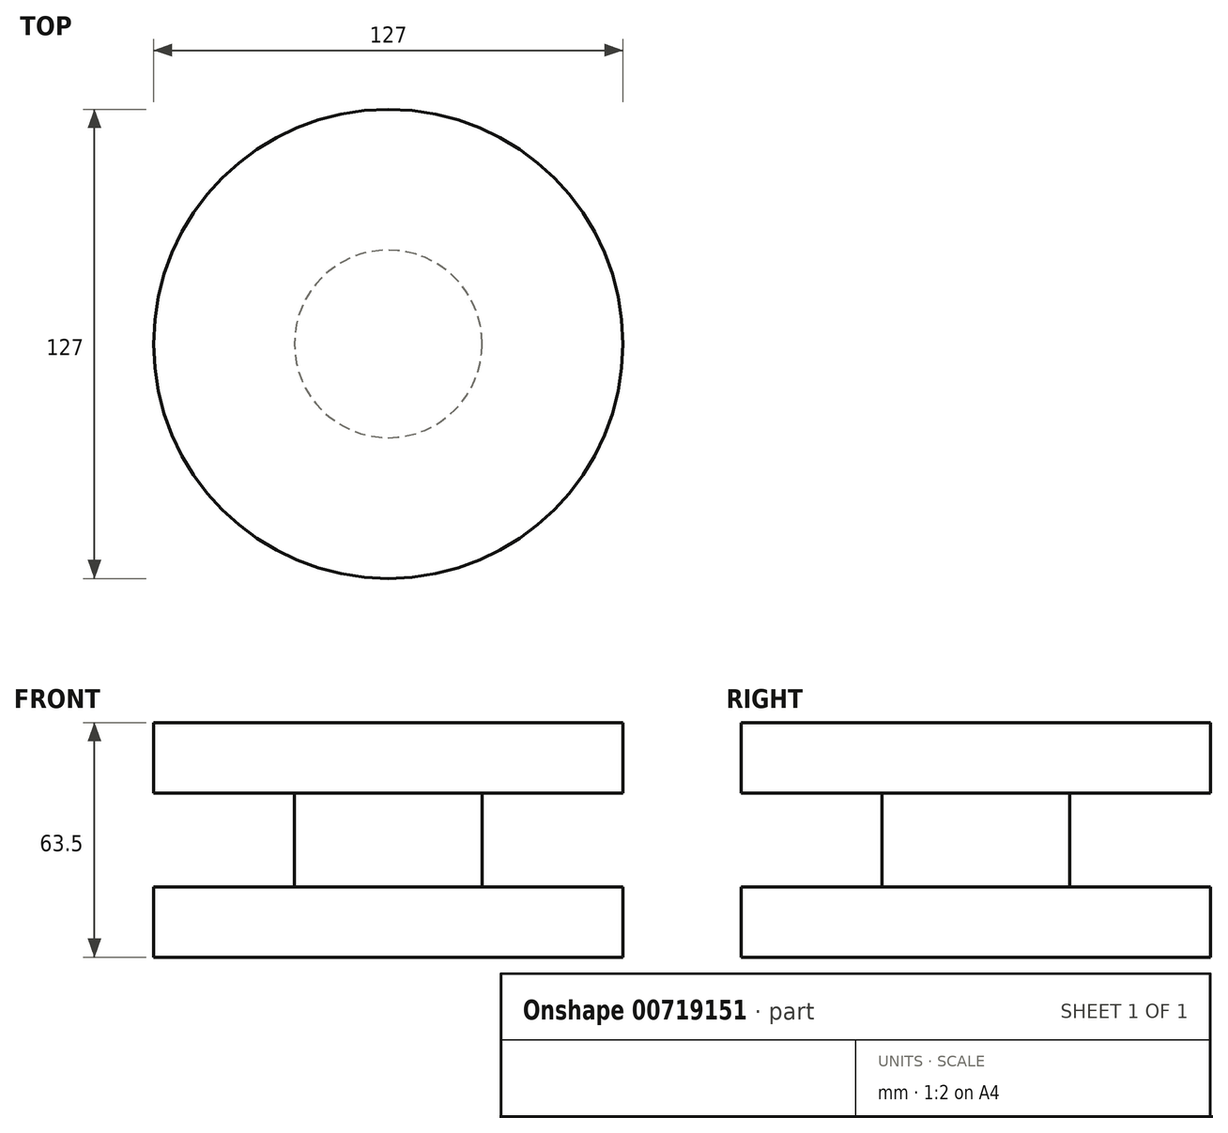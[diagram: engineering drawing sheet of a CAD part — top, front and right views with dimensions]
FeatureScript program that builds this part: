
annotation { "Feature Type Name" : "Feature", "Feature Type Description" : "" }
export const myFeature = defineFeature(function(context is Context, id is Id, definition is map)
    precondition{}
    {
        {
            var Q0;
            Q0=qCreatedBy(makeId("Top.planeOp"),FACE);
            var sketch = newSketch(context, id + "F0", { "sketchPlane" : qUnion([Q0])});
            skCircle(sketch, "E0", {"center": v(0, 0) * mm, "radius": 63.5 * mm});
            skSolve(sketch);
        }
        {
            var Q0;
            Q0=makeQuery(id+"F0.imprint","IMPRINT",FACE,{"disambiguationData":[TD([[makeQuery(id+"F0.imprint","IMPRINT",EDGE,{"derivedFrom":sQuery(id+"F0.wireOp",EDGE,"E0")}),1.0]])]});
            extrude(context, id + "F1", {"entities" : qUnion([Q0]), "depth" : 63.5 * mm, "offsetDistance" : 25.4 * mm});
        }
        {
            var Q0;
            Q0=qCreatedBy(makeId("Front.planeOp"),FACE);
            var sketch = newSketch(context, id + "F2", { "sketchPlane" : qUnion([Q0])});
            skLineSegment(sketch, "E1", {"start": v(0, 0) * mm, "end": v(-63.5, 0) * mm});
            skLineSegment(sketch, "E2", {"start": v(-63.5, 0) * mm, "end": v(-63.5, 19.05) * mm});
            skLineSegment(sketch, "E3.bottom", {"start": v(-63.5, 19.05) * mm, "end": v(-25.4, 19.05) * mm});
            skLineSegment(sketch, "E3.top", {"start": v(-63.5, 44.45) * mm, "end": v(-25.4, 44.45) * mm});
            skLineSegment(sketch, "E3.left", {"start": v(-63.5, 19.05) * mm, "end": v(-63.5, 44.45) * mm});
            skLineSegment(sketch, "E3.right", {"start": v(-25.4, 19.05) * mm, "end": v(-25.4, 44.45) * mm});
            skLineSegment(sketch, "E4", {"start": v(0, 0) * mm, "end": v(0, 63.5) * mm});
            skSolve(sketch);
        }
        {
            var Q0;
            Q0 = qSketchRegion(id + "F2", true);
            var Q1;
            Q1=sQuery(id+"F2.wireOp",EDGE,"E3.left");
            var Q2;
            Q2=sQuery(id+"F2.wireOp",EDGE,"E3.bottom");
            var Q3;
            Q3=sQuery(id+"F2.wireOp",EDGE,"E3.right");
            var Q4;
            Q4=sQuery(id+"F2.wireOp",EDGE,"E3.top");
            var Q5;
            Q5=sQuery(id+"F2.wireOp",EDGE,"E4");
            revolve(context, id + "F3", {"operationType" : NewBodyOperationType.REMOVE, "surfaceOperationType" : NewSurfaceOperationType.NEW, "entities" : qUnion([Q0]), "surfaceEntities" : qUnion([Q1, Q2, Q3, Q4]), "axis" : qUnion([Q5]), "revolveType" : RevolveType.FULL});
        }
    });
